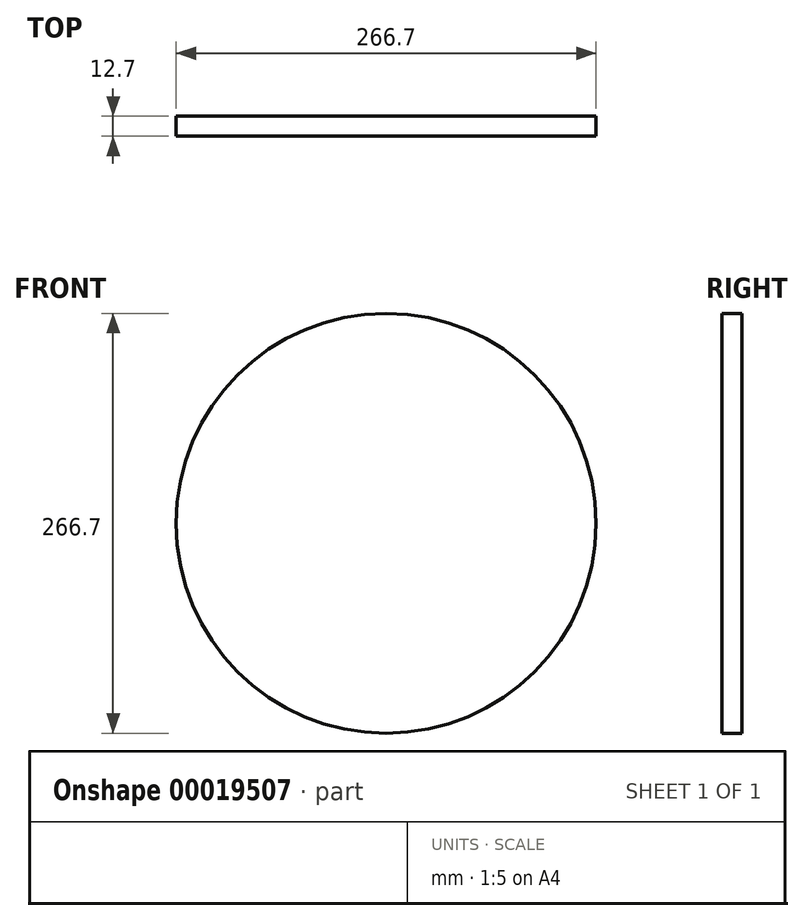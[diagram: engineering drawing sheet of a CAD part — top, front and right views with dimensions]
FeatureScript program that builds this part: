
annotation { "Feature Type Name" : "Feature", "Feature Type Description" : "" }
export const myFeature = defineFeature(function(context is Context, id is Id, definition is map)
    precondition{}
    {
        {
            var Q0;
            Q0=qCreatedBy(makeId("Front.planeOp"),FACE);
            var sketch = newSketch(context, id + "F0", { "sketchPlane" : qUnion([Q0])});
            skCircle(sketch, "E0", {"center": v(0, 0) * mm, "radius": 133.35 * mm});
            skSolve(sketch);
        }
        {
            var Q0;
            Q0 = qSketchRegion(id + "F0", true);
            extrude(context, id + "F1", {"entities" : qUnion([Q0]), "depth" : 12.7 * mm});
        }
    });
